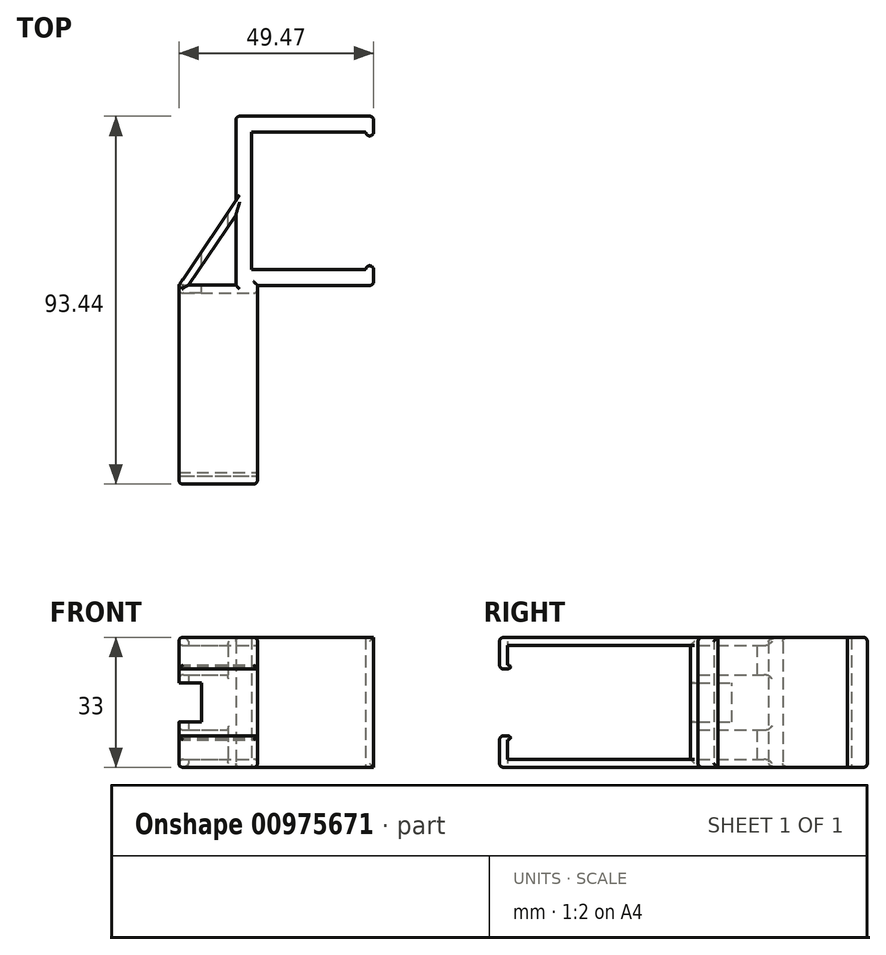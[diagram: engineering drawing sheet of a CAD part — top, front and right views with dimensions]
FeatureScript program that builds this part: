
annotation { "Feature Type Name" : "Feature", "Feature Type Description" : "" }
export const myFeature = defineFeature(function(context is Context, id is Id, definition is map)
    precondition{}
    {
        {
            var Q0;
            Q0=qCreatedBy(makeId("Right.planeOp"),FACE);
            var sketch = newSketch(context, id + "F0", { "sketchPlane" : qUnion([Q0])});
            skLineSegment(sketch, "E0", {"start": v(-78.4, 25) * mm, "end": v(-78.4, 33) * mm});
            skLineSegment(sketch, "E1", {"start": v(-78.4, 33) * mm, "end": v(-27.9, 33) * mm});
            skLineSegment(sketch, "E2", {"start": v(-27.9, 33) * mm, "end": v(-27.9, 0) * mm});
            skLineSegment(sketch, "E3", {"start": v(-27.9, 0) * mm, "end": v(-78.4, 0) * mm});
            skLineSegment(sketch, "E4", {"start": v(-78.4, 0) * mm, "end": v(-78.4, 8) * mm});
            skLineSegment(sketch, "E5", {"start": v(-78.4, 8) * mm, "end": v(-76.4, 8) * mm});
            skLineSegment(sketch, "E6", {"start": v(-76.4, 8) * mm, "end": v(-76.4, 2) * mm});
            skLineSegment(sketch, "E7", {"start": v(-76.4, 2) * mm, "end": v(-29.9, 2) * mm});
            skLineSegment(sketch, "E8", {"start": v(-29.9, 2) * mm, "end": v(-29.9, 31) * mm});
            skLineSegment(sketch, "E9", {"start": v(-29.9, 31) * mm, "end": v(-76.4, 31) * mm});
            skLineSegment(sketch, "E10", {"start": v(-76.4, 31) * mm, "end": v(-76.4, 25) * mm});
            skLineSegment(sketch, "E11", {"start": v(-76.4, 25) * mm, "end": v(-78.4, 25) * mm});
            skLineSegment(sketch, "E12", {"start": v(-76.4, 8) * mm, "end": v(-75.4, 8) * mm});
            skLineSegment(sketch, "E13", {"start": v(-75.4, 8) * mm, "end": v(-75.4, 7) * mm});
            skLineSegment(sketch, "E14", {"start": v(-75.4, 7) * mm, "end": v(-76.4, 7) * mm});
            skLineSegment(sketch, "E15", {"start": v(-76.4, 25) * mm, "end": v(-75.4, 25) * mm});
            skLineSegment(sketch, "E16", {"start": v(-75.4, 25) * mm, "end": v(-75.4, 26) * mm});
            skLineSegment(sketch, "E17", {"start": v(-75.4, 26) * mm, "end": v(-76.4, 26) * mm});
            skSolve(sketch);
        }
        {
            var Q0;
            Q0 = qSketchRegion(id + "F0", true);
            extrude(context, id + "F1", {"entities" : qUnion([Q0]), "oppositeDirection" : true, "depth" : 20 * mm, "offsetDistance" : 25 * mm});
        }
        {
            var Q0;
            Q0=qCreatedBy(makeId("Top.planeOp"),FACE);
            var sketch = newSketch(context, id + "F2", { "sketchPlane" : qUnion([Q0])});
            skLineSegment(sketch, "E18", {"start": v(29.47, 15.04) * mm, "end": v(29.47, 11.04) * mm});
            skLineSegment(sketch, "E19", {"start": v(29.47, 11.04) * mm, "end": v(-1.53, 11.04) * mm});
            skLineSegment(sketch, "E20", {"start": v(-1.53, 11.04) * mm, "end": v(-1.53, -23.96) * mm});
            skLineSegment(sketch, "E21", {"start": v(-1.53, -23.96) * mm, "end": v(29.47, -23.96) * mm});
            skLineSegment(sketch, "E22", {"start": v(29.47, -23.96) * mm, "end": v(29.47, -27.96) * mm});
            skLineSegment(sketch, "E23", {"start": v(29.47, -27.96) * mm, "end": v(-5.53, -27.96) * mm});
            skLineSegment(sketch, "E24", {"start": v(-5.53, -27.96) * mm, "end": v(-5.53, 15.04) * mm});
            skLineSegment(sketch, "E25", {"start": v(-5.53, 15.04) * mm, "end": v(29.47, 15.04) * mm});
            skLineSegment(sketch, "E26.bottom", {"start": v(29.47, -23.96) * mm, "end": v(27.47, -23.96) * mm});
            skLineSegment(sketch, "E26.top", {"start": v(29.47, -22.96) * mm, "end": v(27.47, -22.96) * mm});
            skLineSegment(sketch, "E26.left", {"start": v(29.47, -23.96) * mm, "end": v(29.47, -22.96) * mm});
            skLineSegment(sketch, "E26.right", {"start": v(27.47, -23.96) * mm, "end": v(27.47, -22.96) * mm});
            skLineSegment(sketch, "E27.bottom", {"start": v(29.47, 11.04) * mm, "end": v(27.47, 11.04) * mm});
            skLineSegment(sketch, "E27.top", {"start": v(29.47, 10.04) * mm, "end": v(27.47, 10.04) * mm});
            skLineSegment(sketch, "E27.left", {"start": v(29.47, 11.04) * mm, "end": v(29.47, 10.04) * mm});
            skLineSegment(sketch, "E27.right", {"start": v(27.47, 11.04) * mm, "end": v(27.47, 10.04) * mm});
            skPoint(sketch, "E28", {"position": v(-5.53, -6.46) * mm});
            skLineSegment(sketch, "E29", {"start": v(-2.03, -36.98) * mm, "end": v(-2.03, 32.75) * mm, "construction": true});
            skPoint(sketch, "E30", {"position": v(-2.03, 15.04) * mm});
            skSolve(sketch);
        }
        {
            var Q0;
            {var subQ3=sQuery(id+"F2.wireOp",EDGE,"E18");Q0=qUnion([makeQuery(id+"F2.imprint","IMPRINT",FACE,{"disambiguationData":[TD([[makeQuery(id+"F2.imprint","IMPRINT",EDGE,{"derivedFrom":sQuery(id+"F2.wireOp",EDGE,"E27.top")}),-1.0]])]}),makeQuery(id+"F2.imprint","IMPRINT",FACE,{"disambiguationData":[TD([[makeQuery(id+"F2.imprint","IMPRINT",EDGE,{"derivedFrom":sQuery(id+"F2.wireOp",EDGE,"E26.top")}),1.0]])]}),makeQuery(id+"F2.imprint","IMPRINT",FACE,{"disambiguationData":[TD([[makeQuery(id+"F2.imprint","IMPRINT",EDGE,{"derivedFrom":subQ3}),-1.0]])]})]);}
            var Q1;
            Q1=makeQuery(id+"F1.opExtrude","SWEPT_FACE",FACE,{"disambiguationData":[OSD([sQuery(id+"F0.wireOp",EDGE,"E1")])]});
            extrude(context, id + "F3", {"entities" : qUnion([Q0]), "endBound" : BoundingType.UP_TO_SURFACE, "depth" : 25 * mm, "endBoundEntityFace" : qUnion([Q1]), "offsetDistance" : 25 * mm});
        }
        {
            var Q0;
            Q0=qCreatedBy(makeId("Top.planeOp"),FACE);
            var sketch = newSketch(context, id + "F4", { "sketchPlane" : qUnion([Q0])});
            skLineSegment(sketch, "E31", {"start": v(-20, -27.9) * mm, "end": v(-5.53, -6.46) * mm});
            skLineSegment(sketch, "E32.0", {"start": v(-17.59, -27.9) * mm, "end": v(-5.53, -10.04) * mm});
            skLineSegment(sketch, "E33", {"start": v(-5.53, -6.46) * mm, "end": v(-5.53, -10.04) * mm});
            skLineSegment(sketch, "E34", {"start": v(-17.59, -27.9) * mm, "end": v(-20, -27.9) * mm});
            skSolve(sketch);
        }
        {
            var Q0;
            Q0=makeQuery(id+"F4.imprint","IMPRINT",FACE,{"disambiguationData":[TD([[makeQuery(id+"F4.imprint","IMPRINT",EDGE,{"derivedFrom":sQuery(id+"F4.wireOp",EDGE,"E31")}),-1.0]])]});
            var Q1;
            Q1=makeQuery(id+"F3.opExtrude","CAP_FACE",FACE,{"disambiguationData":[OSD([sQuery(id+"F2.wireOp",EDGE,"E18"),sQuery(id+"F2.wireOp",EDGE,"E19"),sQuery(id+"F2.wireOp",EDGE,"E20"),sQuery(id+"F2.wireOp",EDGE,"E21"),sQuery(id+"F2.wireOp",EDGE,"E22"),sQuery(id+"F2.wireOp",EDGE,"E23"),sQuery(id+"F2.wireOp",EDGE,"E24"),sQuery(id+"F2.wireOp",EDGE,"E25"),sQuery(id+"F2.wireOp",EDGE,"E26.top"),sQuery(id+"F2.wireOp",EDGE,"E26.left"),sQuery(id+"F2.wireOp",EDGE,"E26.right"),sQuery(id+"F2.wireOp",EDGE,"E27.top"),sQuery(id+"F2.wireOp",EDGE,"E27.left"),sQuery(id+"F2.wireOp",EDGE,"E27.right")])],"isStart":false});
            extrude(context, id + "F5", {"entities" : qUnion([Q0]), "operationType" : NewBodyOperationType.ADD, "endBound" : BoundingType.UP_TO_SURFACE, "depth" : 25 * mm, "endBoundEntityFace" : qUnion([Q1]), "offsetDistance" : 25 * mm});
        }
        {
            var Q0;
            Q0=qCreatedBy(makeId("Front.planeOp"),FACE);
            var sketch = newSketch(context, id + "F6", { "sketchPlane" : qUnion([Q0])});
            skLineSegment(sketch, "E35.bottom", {"start": v(-20, 11.5) * mm, "end": v(-14.23, 11.5) * mm});
            skLineSegment(sketch, "E35.top", {"start": v(-20, 21.5) * mm, "end": v(-14.23, 21.5) * mm});
            skLineSegment(sketch, "E35.left", {"start": v(-20, 11.5) * mm, "end": v(-20, 21.5) * mm});
            skLineSegment(sketch, "E35.right", {"start": v(-14.23, 11.5) * mm, "end": v(-14.23, 21.5) * mm});
            skPoint(sketch, "E36", {"position": v(-20, 16.5) * mm});
            skLineSegment(sketch, "E37", {"start": v(0, 0) * mm, "end": v(0, 29.05) * mm, "construction": true});
            skLineSegment(sketch, "E38", {"start": v(-45.08, 14.53) * mm, "end": v(42.15, 14.53) * mm, "construction": true});
            skPoint(sketch, "E38.startSnap0", {"position": v(0, 14.53) * mm});
            skLineSegment(sketch, "E39.0", {"start": v(-20, 33) * mm, "end": v(-20, 0) * mm, "construction": true});
            skLineSegment(sketch, "E40.bottom", {"start": v(-20, 31) * mm, "end": v(-7.53, 31) * mm});
            skLineSegment(sketch, "E40.top", {"start": v(-20, 2) * mm, "end": v(-7.53, 2) * mm});
            skLineSegment(sketch, "E40.left", {"start": v(-20, 31) * mm, "end": v(-20, 2) * mm});
            skLineSegment(sketch, "E40.right", {"start": v(-7.53, 31) * mm, "end": v(-7.53, 2) * mm});
            skLineSegment(sketch, "E41.bottom", {"start": v(-20, 21.5) * mm, "end": v(-7.53, 21.5) * mm});
            skLineSegment(sketch, "E41.top", {"start": v(-20, 23.5) * mm, "end": v(-7.53, 23.5) * mm});
            skLineSegment(sketch, "E41.left", {"start": v(-20, 21.5) * mm, "end": v(-20, 23.5) * mm});
            skLineSegment(sketch, "E41.right", {"start": v(-7.53, 21.5) * mm, "end": v(-7.53, 23.5) * mm});
            skLineSegment(sketch, "E42.bottom", {"start": v(-20, 11.5) * mm, "end": v(-7.53, 11.5) * mm});
            skLineSegment(sketch, "E42.top", {"start": v(-20, 9.5) * mm, "end": v(-7.53, 9.5) * mm});
            skLineSegment(sketch, "E42.left", {"start": v(-20, 11.5) * mm, "end": v(-20, 9.5) * mm});
            skLineSegment(sketch, "E42.right", {"start": v(-7.53, 11.5) * mm, "end": v(-7.53, 9.5) * mm});
            skSolve(sketch);
        }
        {
            var Q0;
            {var subQ0=sQuery(id+"F6.wireOp",EDGE,"E40.bottom");Q0=makeQuery(id+"F6.imprint","IMPRINT",FACE,{"disambiguationData":[TD([[makeQuery(id+"F6.imprint","IMPRINT",EDGE,{"derivedFrom":subQ0}),-1.0]])]});}
            var Q1;
            {var subQ0=sQuery(id+"F6.wireOp",EDGE,"E40.top");Q1=makeQuery(id+"F6.imprint","IMPRINT",FACE,{"disambiguationData":[TD([[makeQuery(id+"F6.imprint","IMPRINT",EDGE,{"derivedFrom":subQ0}),1.0]])]});}
            var Q2;
            {var subQ1=sQuery(id+"F4.wireOp",EDGE,"easG5ne8-TJlI-4DbP-fpjM-Q43OnXX2GBl7");var subQ6=sQuery(id+"F0.wireOp",EDGE,"E2");Q2=makeQuery(id+"F5.boolean.opBoolean","SPLIT",FACE,{"disambiguationData":[TD([makeQuery(id+"F5.opExtrude","SWEPT_FACE",FACE,{"disambiguationData":[OSD([subQ1])]})])],"derivedFrom":makeQuery(id+"F1.opExtrude","SWEPT_FACE",FACE,{"disambiguationData":[OSD([subQ6])]})});}
            extrude(context, id + "F7", {"entities" : qUnion([Q0, Q1]), "operationType" : NewBodyOperationType.REMOVE, "endBound" : BoundingType.UP_TO_SURFACE, "depth" : 30.2 * mm, "endBoundEntityFace" : qUnion([Q2]), "offsetDistance" : 25 * mm});
        }
        {
            var Q0;
            Q0=makeQuery(id+"F6.imprint","IMPRINT",FACE,{"disambiguationData":[TD([[makeQuery(id+"F6.imprint","IMPRINT",EDGE,{"derivedFrom":sQuery(id+"F6.wireOp",EDGE,"E35.bottom")}),1.0]])]});
            var Q1;
            Q1=makeQuery(id+"F1.opExtrude","SWEPT_FACE",FACE,{"disambiguationData":[OSD([sQuery(id+"F0.wireOp",EDGE,"E8")])]});
            extrude(context, id + "F8", {"entities" : qUnion([Q0]), "operationType" : NewBodyOperationType.REMOVE, "endBound" : BoundingType.UP_TO_SURFACE, "depth" : 25 * mm, "endBoundEntityFace" : qUnion([Q1]), "offsetDistance" : 25 * mm});
        }
        {
            var Q0;
            Q0=makeQuery(id+"F3.opExtrude","SWEPT_EDGE",EDGE,{"disambiguationData":[OSD([sQuery(id+"F2.wireOp",EDGE,"E26.top"),sQuery(id+"F2.wireOp",EDGE,"E26.right")])]});
            var Q1;
            Q1=makeQuery(id+"F3.opExtrude","SWEPT_EDGE",EDGE,{"disambiguationData":[OSD([sQuery(id+"F2.wireOp",EDGE,"E26.top"),sQuery(id+"F2.wireOp",EDGE,"E26.left")])]});
            var Q2;
            Q2=makeQuery(id+"F3.opExtrude","SWEPT_EDGE",EDGE,{"disambiguationData":[OSD([sQuery(id+"F2.wireOp",EDGE,"E27.top"),sQuery(id+"F2.wireOp",EDGE,"E27.left")])]});
            var Q3;
            Q3=makeQuery(id+"F3.opExtrude","SWEPT_EDGE",EDGE,{"disambiguationData":[OSD([sQuery(id+"F2.wireOp",EDGE,"E27.top"),sQuery(id+"F2.wireOp",EDGE,"E27.right")])]});
            var Q4;
            Q4=makeQuery(id+"F3.opExtrude","SWEPT_EDGE",EDGE,{"disambiguationData":[OSD([sQuery(id+"F2.wireOp",EDGE,"E22"),sQuery(id+"F2.wireOp",EDGE,"E23")])]});
            var Q5;
            Q5=makeQuery(id+"F3.opExtrude","CAP_EDGE",EDGE,{"disambiguationData":[OSD([sQuery(id+"F2.wireOp",EDGE,"E23")])],"isStart":false});
            var Q6;
            Q6=makeQuery(id+"F3.opExtrude","CAP_EDGE",EDGE,{"disambiguationData":[OSD([sQuery(id+"F2.wireOp",EDGE,"E22"),sQuery(id+"F2.wireOp",EDGE,"E26.left")])],"isStart":false});
            var Q7;
            Q7=makeQuery(id+"F3.opExtrude","CAP_EDGE",EDGE,{"disambiguationData":[OSD([sQuery(id+"F2.wireOp",EDGE,"E23")])],"isStart":true});
            var Q8;
            Q8=makeQuery(id+"F3.opExtrude","CAP_EDGE",EDGE,{"disambiguationData":[OSD([sQuery(id+"F2.wireOp",EDGE,"E25")])],"isStart":true});
            var Q9;
            Q9=makeQuery(id+"F3.opExtrude","SWEPT_EDGE",EDGE,{"disambiguationData":[OSD([sQuery(id+"F2.wireOp",EDGE,"E18"),sQuery(id+"F2.wireOp",EDGE,"E25")])]});
            var Q10;
            Q10=makeQuery(id+"F3.opExtrude","CAP_EDGE",EDGE,{"disambiguationData":[OSD([sQuery(id+"F2.wireOp",EDGE,"E25")])],"isStart":false});
            var Q11;
            Q11=makeQuery(id+"F3.opExtrude","SWEPT_EDGE",EDGE,{"disambiguationData":[OSD([sQuery(id+"F2.wireOp",EDGE,"E24"),sQuery(id+"F2.wireOp",EDGE,"E25")])]});
            var Q12;
            Q12=makeQuery(id+"F1.opExtrude","SWEPT_EDGE",EDGE,{"disambiguationData":[OSD([sQuery(id+"F0.wireOp",EDGE,"E2"),sQuery(id+"F0.wireOp",EDGE,"E3")])]});
            var Q13;
            Q13=makeQuery(id+"F3.opExtrude","CAP_EDGE",EDGE,{"disambiguationData":[OSD([sQuery(id+"F2.wireOp",EDGE,"E24")])],"isStart":true});
            var Q14;
            Q14=makeQuery(id+"F5.opExtrude","CAP_EDGE",EDGE,{"disambiguationData":[OSD([sQuery(id+"F4.wireOp",EDGE,"E33")])],"isStart":true});
            var Q15;
            Q15=makeQuery(id+"F3.opExtrude","CAP_EDGE",EDGE,{"disambiguationData":[OSD([sQuery(id+"F2.wireOp",EDGE,"E24")])],"isStart":false});
            var Q16;
            Q16=makeQuery(id+"F5.opExtrude","CAP_EDGE",EDGE,{"disambiguationData":[OSD([sQuery(id+"F4.wireOp",EDGE,"E33")])],"isStart":false});
            var Q17;
            Q17=makeQuery(id+"F7.boolean.opBoolean","INTERSECT",EDGE,{"derivedFrom":[makeQuery(id+"F5.opExtrude","SWEPT_FACE",FACE,{"disambiguationData":[OSD([sQuery(id+"F4.wireOp",EDGE,"E31")])]}),makeQuery(id+"F7.opExtrude","SWEPT_FACE",FACE,{"disambiguationData":[OSD([sQuery(id+"F6.wireOp",EDGE,"E41.top")])]})]});
            var Q18;
            {var subQ0=sQuery(id+"F6.wireOp",EDGE,"E40.right");Q18=makeQuery(id+"F7.boolean.opBoolean","INTERSECT",EDGE,{"derivedFrom":[makeQuery(id+"F5.opExtrude","SWEPT_FACE",FACE,{"disambiguationData":[OSD([sQuery(id+"F4.wireOp",EDGE,"E31")])]}),makeQuery(id+"F7.opExtrude","SWEPT_FACE",FACE,{"disambiguationData":[OSD([subQ0]),TDD([makeQuery(id+"F6.imprint","IMPRINT",EDGE,{"disambiguationData":[TD([[makeQuery(id+"F6.imprint","INTERSECT",VERTEX,{"derivedFrom":[sQuery(id+"F6.wireOp",EDGE,"E40.bottom"),subQ0]}),-1.0]])],"derivedFrom":subQ0})])]})]});}
            var Q19;
            Q19=makeQuery(id+"F7.boolean.opBoolean","INTERSECT",EDGE,{"derivedFrom":[makeQuery(id+"F5.opExtrude","SWEPT_FACE",FACE,{"disambiguationData":[OSD([sQuery(id+"F4.wireOp",EDGE,"E31")])]}),makeQuery(id+"F7.opExtrude","SWEPT_FACE",FACE,{"disambiguationData":[OSD([sQuery(id+"F6.wireOp",EDGE,"E40.bottom")])]})]});
            var Q20;
            Q20=makeQuery(id+"F7.boolean.opBoolean","INTERSECT",EDGE,{"derivedFrom":[makeQuery(id+"F5.opExtrude","SWEPT_FACE",FACE,{"disambiguationData":[OSD([sQuery(id+"F4.wireOp",EDGE,"E31")])]}),makeQuery(id+"F7.opExtrude","SWEPT_FACE",FACE,{"disambiguationData":[OSD([sQuery(id+"F6.wireOp",EDGE,"E42.top")])]})]});
            var Q21;
            {var subQ0=sQuery(id+"F6.wireOp",EDGE,"E40.right");Q21=makeQuery(id+"F7.boolean.opBoolean","INTERSECT",EDGE,{"derivedFrom":[makeQuery(id+"F5.opExtrude","SWEPT_FACE",FACE,{"disambiguationData":[OSD([sQuery(id+"F4.wireOp",EDGE,"E31")])]}),makeQuery(id+"F7.opExtrude","SWEPT_FACE",FACE,{"disambiguationData":[OSD([subQ0]),TDD([makeQuery(id+"F6.imprint","IMPRINT",EDGE,{"disambiguationData":[TD([[makeQuery(id+"F6.imprint","INTERSECT",VERTEX,{"derivedFrom":[sQuery(id+"F6.wireOp",EDGE,"E40.top"),subQ0]}),1.0]])],"derivedFrom":subQ0})])]})]});}
            var Q22;
            Q22=makeQuery(id+"F7.boolean.opBoolean","INTERSECT",EDGE,{"derivedFrom":[makeQuery(id+"F5.opExtrude","SWEPT_FACE",FACE,{"disambiguationData":[OSD([sQuery(id+"F4.wireOp",EDGE,"E31")])]}),makeQuery(id+"F7.opExtrude","SWEPT_FACE",FACE,{"disambiguationData":[OSD([sQuery(id+"F6.wireOp",EDGE,"E40.top")])]})]});
            var Q23;
            Q23=makeQuery(id+"F5.opExtrude","CAP_EDGE",EDGE,{"disambiguationData":[OSD([sQuery(id+"F4.wireOp",EDGE,"E32.0")])],"isStart":true});
            var Q24;
            Q24=makeQuery(id+"F5.opExtrude","CAP_EDGE",EDGE,{"disambiguationData":[OSD([sQuery(id+"F4.wireOp",EDGE,"E32.0")])],"isStart":false});
            var Q25;
            Q25=makeQuery(id+"F8.boolean.opBoolean","COPY",EDGE,{"derivedFrom":makeQuery(id+"F8.opExtrude","CAP_EDGE",EDGE,{"disambiguationData":[OSD([sQuery(id+"F6.wireOp",EDGE,"E35.right")])],"isStart":false})});
            var Q26;
            {var subQ0=sQuery(id+"F0.wireOp",EDGE,"E9");var subQ1=sQuery(id+"F0.wireOp",EDGE,"E8");Q26=makeQuery(id+"F8.boolean.opBoolean","SPLIT",EDGE,{"disambiguationData":[TD([makeQuery(id+"F1.opExtrude","SWEPT_FACE",FACE,{"disambiguationData":[OSD([subQ0])]})])],"derivedFrom":makeQuery(id+"F1.opExtrude","CAP_EDGE",EDGE,{"disambiguationData":[OSD([subQ1])],"isStart":false})});}
            var Q27;
            {var subQ0=sQuery(id+"F0.wireOp",EDGE,"E8");var subQ1=sQuery(id+"F0.wireOp",EDGE,"E7");Q27=makeQuery(id+"F8.boolean.opBoolean","SPLIT",EDGE,{"disambiguationData":[TD([makeQuery(id+"F1.opExtrude","SWEPT_FACE",FACE,{"disambiguationData":[OSD([subQ1])]})])],"derivedFrom":makeQuery(id+"F1.opExtrude","CAP_EDGE",EDGE,{"disambiguationData":[OSD([subQ0])],"isStart":false})});}
            var Q28;
            Q28=makeQuery(id+"F8.boolean.opBoolean","COPY",EDGE,{"derivedFrom":makeQuery(id+"F8.opExtrude","CAP_EDGE",EDGE,{"disambiguationData":[OSD([sQuery(id+"F6.wireOp",EDGE,"E35.bottom")])],"isStart":false})});
            var Q29;
            Q29=makeQuery(id+"F8.boolean.opBoolean","COPY",EDGE,{"derivedFrom":makeQuery(id+"F8.opExtrude","CAP_EDGE",EDGE,{"disambiguationData":[OSD([sQuery(id+"F6.wireOp",EDGE,"E35.top")])],"isStart":false})});
            var Q30;
            Q30=makeQuery(id+"F1.opExtrude","CAP_EDGE",EDGE,{"disambiguationData":[OSD([sQuery(id+"F0.wireOp",EDGE,"E7")])],"isStart":false});
            var Q31;
            Q31=makeQuery(id+"F1.opExtrude","CAP_EDGE",EDGE,{"disambiguationData":[OSD([sQuery(id+"F0.wireOp",EDGE,"E9")])],"isStart":false});
            var Q32;
            Q32=makeQuery(id+"F1.opExtrude","SWEPT_EDGE",EDGE,{"disambiguationData":[OSD([sQuery(id+"F0.wireOp",EDGE,"E1"),sQuery(id+"F0.wireOp",EDGE,"E2")])]});
            var Q33;
            Q33=makeQuery(id+"F1.opExtrude","CAP_EDGE",EDGE,{"disambiguationData":[OSD([sQuery(id+"F0.wireOp",EDGE,"E3")])],"isStart":false});
            var Q34;
            Q34=makeQuery(id+"F1.opExtrude","CAP_EDGE",EDGE,{"disambiguationData":[OSD([sQuery(id+"F0.wireOp",EDGE,"E1")])],"isStart":false});
            var Q35;
            Q35=makeQuery(id+"F1.opExtrude","SWEPT_EDGE",EDGE,{"disambiguationData":[OSD([sQuery(id+"F0.wireOp",EDGE,"E12"),sQuery(id+"F0.wireOp",EDGE,"E13")])]});
            var Q36;
            Q36=makeQuery(id+"F1.opExtrude","SWEPT_EDGE",EDGE,{"disambiguationData":[OSD([sQuery(id+"F0.wireOp",EDGE,"E13"),sQuery(id+"F0.wireOp",EDGE,"E14")])]});
            var Q37;
            Q37=makeQuery(id+"F1.opExtrude","SWEPT_EDGE",EDGE,{"disambiguationData":[OSD([sQuery(id+"F0.wireOp",EDGE,"E15"),sQuery(id+"F0.wireOp",EDGE,"E16")])]});
            var Q38;
            Q38=makeQuery(id+"F1.opExtrude","SWEPT_EDGE",EDGE,{"disambiguationData":[OSD([sQuery(id+"F0.wireOp",EDGE,"E16"),sQuery(id+"F0.wireOp",EDGE,"E17")])]});
            var Q39;
            Q39=makeQuery(id+"F1.opExtrude","CAP_EDGE",EDGE,{"disambiguationData":[OSD([sQuery(id+"F0.wireOp",EDGE,"E0")])],"isStart":false});
            var Q40;
            Q40=makeQuery(id+"F1.opExtrude","SWEPT_EDGE",EDGE,{"disambiguationData":[OSD([sQuery(id+"F0.wireOp",EDGE,"E0"),sQuery(id+"F0.wireOp",EDGE,"E1")])]});
            var Q41;
            Q41=makeQuery(id+"F1.opExtrude","CAP_EDGE",EDGE,{"disambiguationData":[OSD([sQuery(id+"F0.wireOp",EDGE,"E0")])],"isStart":true});
            var Q42;
            Q42=makeQuery(id+"F1.opExtrude","SWEPT_EDGE",EDGE,{"disambiguationData":[OSD([sQuery(id+"F0.wireOp",EDGE,"E0"),sQuery(id+"F0.wireOp",EDGE,"E11")])]});
            var Q43;
            Q43=makeQuery(id+"F1.opExtrude","SWEPT_EDGE",EDGE,{"disambiguationData":[OSD([sQuery(id+"F0.wireOp",EDGE,"E4"),sQuery(id+"F0.wireOp",EDGE,"E5")])]});
            var Q44;
            Q44=makeQuery(id+"F1.opExtrude","CAP_EDGE",EDGE,{"disambiguationData":[OSD([sQuery(id+"F0.wireOp",EDGE,"E4")])],"isStart":true});
            var Q45;
            Q45=makeQuery(id+"F1.opExtrude","SWEPT_EDGE",EDGE,{"disambiguationData":[OSD([sQuery(id+"F0.wireOp",EDGE,"E3"),sQuery(id+"F0.wireOp",EDGE,"E4")])]});
            var Q46;
            Q46=makeQuery(id+"F1.opExtrude","CAP_EDGE",EDGE,{"disambiguationData":[OSD([sQuery(id+"F0.wireOp",EDGE,"E4")])],"isStart":false});
            var Q47;
            Q47=makeQuery(id+"F1.opExtrude","CAP_EDGE",EDGE,{"disambiguationData":[OSD([sQuery(id+"F0.wireOp",EDGE,"E1")])],"isStart":true});
            var Q48;
            Q48=makeQuery(id+"F1.opExtrude","CAP_EDGE",EDGE,{"disambiguationData":[OSD([sQuery(id+"F0.wireOp",EDGE,"E3")])],"isStart":true});
            var Q49;
            Q49=makeQuery(id+"F1.opExtrude","CAP_EDGE",EDGE,{"disambiguationData":[OSD([sQuery(id+"F0.wireOp",EDGE,"E8")])],"isStart":true});
            var Q50;
            Q50=makeQuery(id+"F3.opExtrude","CAP_EDGE",EDGE,{"disambiguationData":[OSD([sQuery(id+"F2.wireOp",EDGE,"E22"),sQuery(id+"F2.wireOp",EDGE,"E26.left")])],"isStart":true});
            fillet(context, id + "F9", {"entities" : qUnion([Q0, Q1, Q2, Q3, Q4, Q5, Q6, Q7, Q8, Q9, Q10, Q11, Q12, Q13, Q14, Q15, Q16, Q17, Q18, Q19, Q20, Q21, Q22, Q23, Q24, Q25, Q26, Q27, Q28, Q29, Q30, Q31, Q32, Q33, Q34, Q35, Q36, Q37, Q38, Q39, Q40, Q41, Q42, Q43, Q44, Q45, Q46, Q47, Q48, Q49, Q50]), "radius" : 1 * mm, "tangentPropagation" : true, "allowEdgeOverflow" : false});
        }
    });
